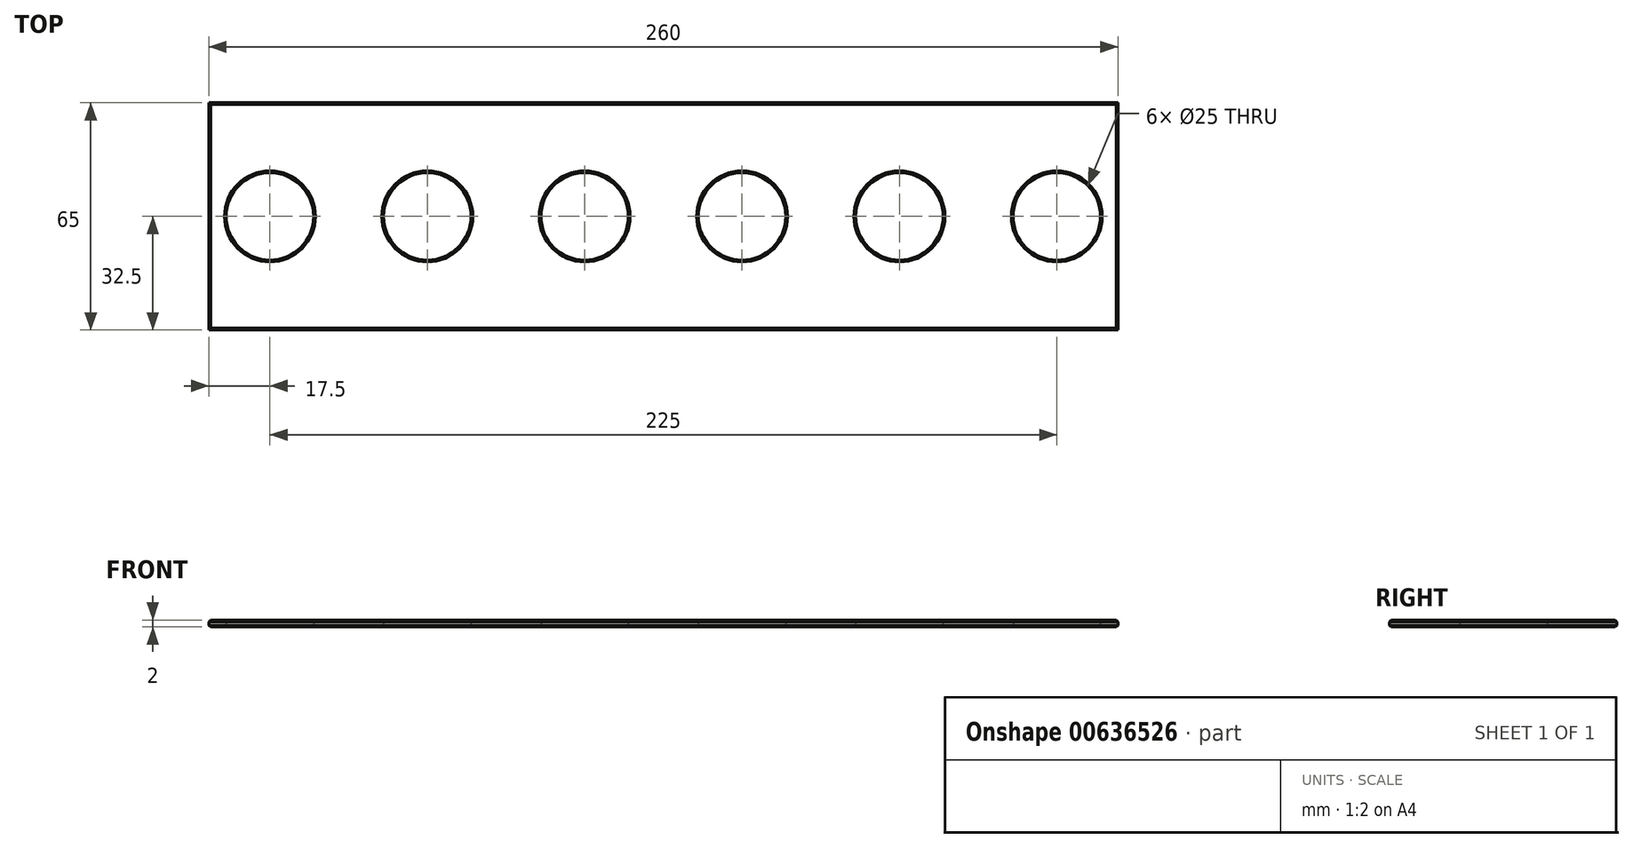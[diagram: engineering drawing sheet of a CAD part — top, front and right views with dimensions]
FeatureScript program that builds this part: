
annotation { "Feature Type Name" : "Feature", "Feature Type Description" : "" }
export const myFeature = defineFeature(function(context is Context, id is Id, definition is map)
    precondition{}
    {
        {
            var Q0;
            Q0=qCreatedBy(makeId("Top.planeOp"),FACE);
            var sketch = newSketch(context, id + "F0", { "sketchPlane" : qUnion([Q0])});
            skLineSegment(sketch, "E0.bottom", {"start": v(0, 0) * mm, "end": v(260, 0) * mm});
            skLineSegment(sketch, "E0.top", {"start": v(0, -65) * mm, "end": v(260, -65) * mm});
            skLineSegment(sketch, "E0.left", {"start": v(0, 0) * mm, "end": v(0, -65) * mm});
            skLineSegment(sketch, "E0.right", {"start": v(260, 0) * mm, "end": v(260, -65) * mm});
            skPoint(sketch, "E1", {"position": v(0, -32.5) * mm});
            skPoint(sketch, "E2", {"position": v(260, -32.5) * mm});
            skLineSegment(sketch, "E3", {"start": v(0, -32.5) * mm, "end": v(260, -32.5) * mm, "construction": true});
            skCircle(sketch, "E4", {"center": v(17.5, -32.5) * mm, "radius": 12.5 * mm});
            skPoint(sketch, "E5", {"position": v(5, -32.5) * mm});
            skLineSegment(sketch, "E6", {"start": v(0, -20) * mm, "end": v(260, -20) * mm, "construction": true});
            skCircle(sketch, "E7", {"center": v(62.5, -32.5) * mm, "radius": 12.5 * mm});
            skCircle(sketch, "E8.1.0.0", {"center": v(107.5, -32.5) * mm, "radius": 12.5 * mm});
            skCircle(sketch, "E8.1.0.1", {"center": v(152.5, -32.5) * mm, "radius": 12.5 * mm});
            skCircle(sketch, "E8.2.0.0", {"center": v(197.5, -32.5) * mm, "radius": 12.5 * mm});
            skCircle(sketch, "E8.2.0.1", {"center": v(242.5, -32.5) * mm, "radius": 12.5 * mm});
            skLineSegment(sketch, "E8.direction1", {"start": v(17.5, -32.5) * mm, "end": v(107.5, -32.5) * mm, "construction": true});
            skSolve(sketch);
        }
        {
            var Q0;
            Q0=makeQuery(id+"F0.imprint","IMPRINT",FACE,{"disambiguationData":[TD([[makeQuery(id+"F0.imprint","IMPRINT",EDGE,{"derivedFrom":sQuery(id+"F0.wireOp",EDGE,"E0.bottom")}),-1.0]])]});
            extrude(context, id + "F1", {"entities" : qUnion([Q0]), "depth" : 2 * mm, "offsetDistance" : 25 * mm});
        }
        {
            var Q0;
            Q0=makeQuery(id+"F1.opExtrude","CAP_FACE",FACE,{"disambiguationData":[OSD([sQuery(id+"F0.wireOp",EDGE,"E0.bottom"),sQuery(id+"F0.wireOp",EDGE,"E0.top"),sQuery(id+"F0.wireOp",EDGE,"E0.left"),sQuery(id+"F0.wireOp",EDGE,"E0.right"),sQuery(id+"F0.wireOp",EDGE,"E4"),sQuery(id+"F0.wireOp",EDGE,"E7"),sQuery(id+"F0.wireOp",EDGE,"E8.1.0.0"),sQuery(id+"F0.wireOp",EDGE,"E8.1.0.1"),sQuery(id+"F0.wireOp",EDGE,"E8.2.0.0"),sQuery(id+"F0.wireOp",EDGE,"E8.2.0.1")])],"isStart":false});
            var Q1;
            Q1=makeQuery(id+"F1.opExtrude","CAP_FACE",FACE,{"disambiguationData":[OSD([sQuery(id+"F0.wireOp",EDGE,"E0.bottom"),sQuery(id+"F0.wireOp",EDGE,"E0.top"),sQuery(id+"F0.wireOp",EDGE,"E0.left"),sQuery(id+"F0.wireOp",EDGE,"E0.right"),sQuery(id+"F0.wireOp",EDGE,"E4"),sQuery(id+"F0.wireOp",EDGE,"E7"),sQuery(id+"F0.wireOp",EDGE,"E8.1.0.0"),sQuery(id+"F0.wireOp",EDGE,"E8.1.0.1"),sQuery(id+"F0.wireOp",EDGE,"E8.2.0.0"),sQuery(id+"F0.wireOp",EDGE,"E8.2.0.1")])],"isStart":true});
            chamfer(context, id + "F2", {"entities" : qUnion([Q0, Q1]), "width" : 0.5 * mm, "tangentPropagation" : true});
        }
    });
